annotation { "Feature Type Name" : "Feature", "Feature Type Description" : "" }
export const myFeature = defineFeature(function(context is Context, id is Id, definition is map)
    precondition{}
    {
        {
            var Q0;
            Q0=qCreatedBy(makeId("Top.planeOp"),FACE);
            var sketch = newSketch(context, id + "F0", { "sketchPlane" : qUnion([Q0])});
            skLineSegment(sketch, "E0.bottom", {"start": v(15000, -25000) * mm, "end": v(-15000, -25000) * mm});
            skLineSegment(sketch, "E0.top", {"start": v(15000, 25000) * mm, "end": v(-15000, 25000) * mm});
            skLineSegment(sketch, "E0.left", {"start": v(15000, -25000) * mm, "end": v(15000, 25000) * mm});
            skLineSegment(sketch, "E0.right", {"start": v(-15000, -25000) * mm, "end": v(-15000, 25000) * mm});
            skPoint(sketch, "E0.middle", {"position": v(0, 0) * mm});
            skSolve(sketch);
        }
        {
            var Q0;
            Q0=makeQuery(id+"F0.imprint","IMPRINT",FACE,{"disambiguationData":[TD([[makeQuery(id+"F0.imprint","IMPRINT",EDGE,{"derivedFrom":sQuery(id+"F0.wireOp",EDGE,"E0.bottom")}),-1.0]])]});
            var Q1;
            Q1=makeQuery(id+"F0.imprint","IMPRINT",FACE,{"disambiguationData":[TD([[makeQuery(id+"F0.imprint","IMPRINT",EDGE,{"derivedFrom":makeQuery(id+"F2.imprint","IMPRINT",EDGE,{"derivedFrom":sQuery(id+"F2.wireOp",EDGE,"E106.sketch_text.stroke-0")})}),-1.0]])]});
            var Q2;
            Q2=makeQuery(id+"F0.imprint","IMPRINT",FACE,{"disambiguationData":[TD([[makeQuery(id+"F0.imprint","IMPRINT",EDGE,{"derivedFrom":makeQuery(id+"F2.imprint","IMPRINT",EDGE,{"derivedFrom":sQuery(id+"F2.wireOp",EDGE,"E106.sketch_text.stroke-63")})}),-1.0]])]});
            var Q3;
            {var subQ5=sQuery(id+"F2.wireOp",EDGE,"E23");Q3=makeQuery(id+"F0.imprint","IMPRINT",FACE,{"disambiguationData":[TD([[makeQuery(id+"F0.imprint","IMPRINT",EDGE,{"derivedFrom":makeQuery(id+"F2.imprint","IMPRINT",EDGE,{"derivedFrom":subQ5})}),-1.0]])]});}
            var Q4;
            Q4=makeQuery(id+"F0.imprint","IMPRINT",FACE,{"disambiguationData":[TD([[makeQuery(id+"F0.imprint","IMPRINT",EDGE,{"derivedFrom":makeQuery(id+"F2.imprint","IMPRINT",EDGE,{"derivedFrom":sQuery(id+"F2.wireOp",EDGE,"E106.sketch_text.stroke-110")})}),-1.0]])]});
            var Q5;
            Q5=makeQuery(id+"F0.imprint","IMPRINT",FACE,{"disambiguationData":[TD([[makeQuery(id+"F0.imprint","IMPRINT",EDGE,{"derivedFrom":makeQuery(id+"F2.imprint","IMPRINT",EDGE,{"derivedFrom":sQuery(id+"F2.wireOp",EDGE,"E106.sketch_text.stroke-133")})}),-1.0]])]});
            var Q6;
            Q6=makeQuery(id+"F0.imprint","IMPRINT",FACE,{"disambiguationData":[TD([[makeQuery(id+"F0.imprint","IMPRINT",EDGE,{"derivedFrom":makeQuery(id+"F2.imprint","IMPRINT",EDGE,{"derivedFrom":sQuery(id+"F2.wireOp",EDGE,"E106.sketch_text.stroke-137")})}),-1.0]])]});
            var Q7;
            Q7=makeQuery(id+"F0.imprint","IMPRINT",FACE,{"disambiguationData":[TD([[makeQuery(id+"F0.imprint","IMPRINT",EDGE,{"derivedFrom":makeQuery(id+"F2.imprint","IMPRINT",EDGE,{"derivedFrom":sQuery(id+"F2.wireOp",EDGE,"E106.sketch_text.stroke-82")})}),-1.0]])]});
            var Q8;
            Q8=makeQuery(id+"F0.imprint","IMPRINT",FACE,{"disambiguationData":[TD([[makeQuery(id+"F0.imprint","IMPRINT",EDGE,{"derivedFrom":makeQuery(id+"F2.imprint","IMPRINT",EDGE,{"derivedFrom":sQuery(id+"F2.wireOp",EDGE,"E106.sketch_text.stroke-38")})}),-1.0]])]});
            var Q9;
            Q9=makeQuery(id+"F0.imprint","IMPRINT",FACE,{"disambiguationData":[TD([[makeQuery(id+"F0.imprint","IMPRINT",EDGE,{"derivedFrom":makeQuery(id+"F2.imprint","IMPRINT",EDGE,{"derivedFrom":sQuery(id+"F2.wireOp",EDGE,"E106.sketch_text.stroke-13")})}),-1.0]])]});
            extrude(context, id + "F1", {"entities" : qUnion([Q0, Q1, Q2, Q3, Q4, Q5, Q6, Q7, Q8, Q9]), "oppositeDirection" : true, "depth" : 25 * mm, "offsetDistance" : 25 * mm});
        }
        {
            var Q0;
            Q0=qCreatedBy(makeId("Top.planeOp"),FACE);
            var sketch = newSketch(context, id + "F2", { "sketchPlane" : qUnion([Q0])});
            skLineSegment(sketch, "E1.bottom", {"start": v(15000, -25000) * mm, "end": v(-15000, -25000) * mm});
            skLineSegment(sketch, "E1.top", {"start": v(15000, 25000) * mm, "end": v(-15000, 25000) * mm});
            skLineSegment(sketch, "E1.left", {"start": v(15000, -25000) * mm, "end": v(15000, 25000) * mm});
            skLineSegment(sketch, "E1.right", {"start": v(-15000, -25000) * mm, "end": v(-15000, -18414.08) * mm});
            skPoint(sketch, "E1.middle", {"position": v(0, 0) * mm});
            skLineSegment(sketch, "E2", {"start": v(15000, 1000) * mm, "end": v(9000, 1000) * mm});
            skLineSegment(sketch, "E3", {"start": v(12185.8, -25000) * mm, "end": v(12185.8, 25000) * mm});
            skLineSegment(sketch, "E4.0", {"start": v(11500, -25000) * mm, "end": v(11500, 25000) * mm});
            skLineSegment(sketch, "E5", {"start": v(9000, -11000) * mm, "end": v(9000, 1000) * mm});
            skLineSegment(sketch, "E6", {"start": v(9000, 1000) * mm, "end": v(9000, 25000) * mm});
            skText(sketch, "E7", { "text": "Weld", "fontName": "OpenSans-Regular.ttf"});
            skText(sketch, "E8", { "text": "Blast", "fontName": "OpenSans-Regular.ttf"});
            skText(sketch, "E9", { "text": "Paint", "fontName": "OpenSans-Regular.ttf"});
            skLineSegment(sketch, "E10", {"start": v(7800, 25000) * mm, "end": v(7800, -25000) * mm});
            skPoint(sketch, "E11.orphan", {"position": v(7800, 25000) * mm});
            skText(sketch, "E12", { "text": "Dock", "fontName": "OpenSans-Regular.ttf"});
            skLineSegment(sketch, "E13", {"start": v(9000, 13000) * mm, "end": v(15000, 13000) * mm});
            skLineSegment(sketch, "E14", {"start": v(3200, 25000) * mm, "end": v(3200, 9000) * mm});
            skPoint(sketch, "E15", {"position": v(800, -25000) * mm});
            skPoint(sketch, "E16", {"position": v(5500, -25000) * mm});
            skLineSegment(sketch, "E17", {"start": v(5157.1, -25000) * mm, "end": v(5157.1, 9000) * mm});
            skLineSegment(sketch, "E18.0", {"start": v(5842.9, -25000) * mm, "end": v(5842.9, 9000) * mm});
            skLineSegment(sketch, "E19.0", {"start": v(-400, 7800) * mm, "end": v(7800, 7800) * mm});
            skPoint(sketch, "E20", {"position": v(-1414.44, -25000) * mm});
            skLineSegment(sketch, "E21", {"start": v(9000, -11000) * mm, "end": v(15000, -11000) * mm});
            skLineSegment(sketch, "E22", {"start": v(-1414.44, -25000) * mm, "end": v(-1414.44, 7800) * mm});
            skLineSegment(sketch, "E23", {"start": v(-1414.44, 7800) * mm, "end": v(-400, 7800) * mm});
            skLineSegment(sketch, "E24.0", {"start": v(-2614.44, -25000) * mm, "end": v(-2614.44, -10700) * mm});
            skLineSegment(sketch, "E25.trimOffspring", {"start": v(3200, 9000) * mm, "end": v(7800, 9000) * mm});
            skPoint(sketch, "E26", {"position": v(-1414.44, -8600) * mm});
            skPoint(sketch, "E27", {"position": v(-1414.44, -8000) * mm});
            skLineSegment(sketch, "E28", {"start": v(-1414.44, -8000) * mm, "end": v(7800, -8000) * mm});
            skLineSegment(sketch, "E29.0", {"start": v(-1414.44, -9200) * mm, "end": v(7800, -9200) * mm});
            skPoint(sketch, "E30", {"position": v(5500, -23850) * mm});
            skLineSegment(sketch, "E31", {"start": v(5500, -23850) * mm, "end": v(4500, -23850) * mm});
            skLineSegment(sketch, "E32", {"start": v(5500, -23850) * mm, "end": v(7500, -23850) * mm});
            skLineSegment(sketch, "E33", {"start": v(4500, -23850) * mm, "end": v(4500, -10350) * mm});
            skLineSegment(sketch, "E34", {"start": v(7500, -23850) * mm, "end": v(7500, -10350) * mm});
            skLineSegment(sketch, "E35", {"start": v(7500, -10350) * mm, "end": v(4500, -10350) * mm});
            skLineSegment(sketch, "E36", {"start": v(-10000, 25000) * mm, "end": v(-10000, 20000) * mm});
            skLineSegment(sketch, "E37", {"start": v(-10000, 20000) * mm, "end": v(-15000, 20000) * mm});
            skText(sketch, "E38", { "text": "Plas", "fontName": "OpenSans-Regular.ttf"});
            skLineSegment(sketch, "E39", {"start": v(-7000, 25000) * mm, "end": v(-7000, 22000) * mm});
            skLineSegment(sketch, "E40", {"start": v(-7000, 22000) * mm, "end": v(-10000, 22000) * mm});
            skText(sketch, "E41", { "text": "Sht.", "fontName": "OpenSans-Regular.ttf"});
            skLineSegment(sketch, "E42", {"start": v(-7000, 22000) * mm, "end": v(-7000, 20000) * mm});
            skLineSegment(sketch, "E43", {"start": v(-15000, 17800) * mm, "end": v(-2452.25, 17800) * mm});
            skLineSegment(sketch, "E44", {"start": v(-10000, 20000) * mm, "end": v(-7000, 20000) * mm});
            skText(sketch, "E45", { "text": "Scp", "fontName": "OpenSans-Regular.ttf"});
            skPoint(sketch, "E46", {"position": v(-15000, 19325) * mm});
            skPoint(sketch, "E47", {"position": v(-15000, 18475) * mm});
            skLineSegment(sketch, "E48", {"start": v(-15000, 18475) * mm, "end": v(-15850, 18475) * mm, "construction": true});
            skArc(sketch, "E49", {"start": v(-15850, 18475) * mm, "mid": v(-15601.04, 19076.04) * mm, "end": v(-15000, 19325) * mm, "construction": true});
            skPoint(sketch, "E50", {"position": v(7975, 25000) * mm});
            skPoint(sketch, "E51", {"position": v(8825, 25000) * mm});
            skLineSegment(sketch, "E52", {"start": v(7975, 25000) * mm, "end": v(7975, 25850) * mm, "construction": true});
            skArc(sketch, "E53", {"start": v(7975, 25850) * mm, "mid": v(8576.04, 25601.04) * mm, "end": v(8825, 25000) * mm, "construction": true});
            skPoint(sketch, "E54", {"position": v(9500, 13000) * mm});
            skPoint(sketch, "E55", {"position": v(14500, 13000) * mm});
            skLineSegment(sketch, "E56", {"start": v(14500, 12500) * mm, "end": v(14500, 13500) * mm, "construction": true});
            skLineSegment(sketch, "E57", {"start": v(9500, 12500) * mm, "end": v(9500, 13500) * mm, "construction": true});
            skLineSegment(sketch, "E58", {"start": v(14500, 24500) * mm, "end": v(14500, 25500) * mm, "construction": true});
            skPoint(sketch, "E59", {"position": v(14500, 25000) * mm});
            skPoint(sketch, "E60", {"position": v(9500, 25000) * mm});
            skLineSegment(sketch, "E61", {"start": v(9500, 24500) * mm, "end": v(9500, 25500) * mm, "construction": true});
            skPoint(sketch, "E62", {"position": v(4200, 25000) * mm});
            skPoint(sketch, "E63", {"position": v(6800, 25000) * mm});
            skLineSegment(sketch, "E64", {"start": v(4200, 24500) * mm, "end": v(4200, 25500) * mm, "construction": true});
            skLineSegment(sketch, "E65", {"start": v(6800, 25000) * mm, "end": v(6800, 24500) * mm, "construction": true});
            skLineSegment(sketch, "E66", {"start": v(6800, 24500) * mm, "end": v(6800, 25500) * mm, "construction": true});
            skLineSegment(sketch, "E67.0", {"start": v(12260.8, -25000) * mm, "end": v(12260.8, 25000) * mm});
            skLineSegment(sketch, "E68.0", {"start": v(11425, -25000) * mm, "end": v(11425, 25000) * mm});
            skLineSegment(sketch, "E69.0", {"start": v(5917.9, -25000) * mm, "end": v(5917.9, 9000) * mm});
            skLineSegment(sketch, "E70.0", {"start": v(5082.1, -25000) * mm, "end": v(5082.1, 9000) * mm});
            skLineSegment(sketch, "E71", {"start": v(-4100.12, 13300) * mm, "end": v(-6825.09, 13300) * mm});
            skPoint(sketch, "E72", {"position": v(-6200, 15550) * mm});
            skLineSegment(sketch, "E73", {"start": v(-6200, 14010) * mm, "end": v(-6200, 17090) * mm});
            skLineSegment(sketch, "E74", {"start": v(-6200, 17090) * mm, "end": v(-8500, 17090) * mm});
            skLineSegment(sketch, "E75", {"start": v(-8500, 17090) * mm, "end": v(-8500, 14010) * mm});
            skLineSegment(sketch, "E76", {"start": v(-8500, 14010) * mm, "end": v(-6200, 14010) * mm});
            skPoint(sketch, "E77", {"position": v(-8500, 15550) * mm});
            skText(sketch, "E78", { "text": "B.Saw", "fontName": "OpenSans-Regular.ttf"});
            skLineSegment(sketch, "E79", {"start": v(-8500, 16050) * mm, "end": v(-14500, 16050) * mm});
            skLineSegment(sketch, "E80", {"start": v(-14500, 16050) * mm, "end": v(-14500, 15550) * mm});
            skLineSegment(sketch, "E81", {"start": v(-14500, 15550) * mm, "end": v(-14500, 15050) * mm});
            skLineSegment(sketch, "E82", {"start": v(-14500, 15050) * mm, "end": v(-8500, 15050) * mm});
            skLineSegment(sketch, "E83", {"start": v(-6200, 16050) * mm, "end": v(-3000, 16050) * mm});
            skLineSegment(sketch, "E84", {"start": v(-6200, 15050) * mm, "end": v(-3000, 15050) * mm});
            skLineSegment(sketch, "E85", {"start": v(-3000, 15050) * mm, "end": v(-3000, 16050) * mm});
            skLineSegment(sketch, "E86", {"start": v(-15000, 9900) * mm, "end": v(-4100.12, 9900) * mm});
            skLineSegment(sketch, "E87", {"start": v(-4100.12, 9900) * mm, "end": v(-4100.12, 13300) * mm});
            skLineSegment(sketch, "E88", {"start": v(-9550.06, 13300) * mm, "end": v(-9550.06, 9900) * mm});
            skLineSegment(sketch, "E89", {"start": v(-9550.06, 13300) * mm, "end": v(-15000, 13300) * mm});
            skLineSegment(sketch, "E90", {"start": v(-6825.09, 13300) * mm, "end": v(-6825.09, 9900) * mm});
            skLineSegment(sketch, "E91", {"start": v(-6825.09, 13300) * mm, "end": v(-9550.06, 13300) * mm});
            skText(sketch, "E92", { "text": "Mess", "fontName": "OpenSans-Regular.ttf"});
            skText(sketch, "E93", { "text": "Office", "fontName": "OpenSans-Regular.ttf"});
            skText(sketch, "E94", { "text": "Office", "fontName": "OpenSans-Regular.ttf"});
            skLineSegment(sketch, "E95", {"start": v(-15000, 5100) * mm, "end": v(-10300, 5100) * mm});
            skLineSegment(sketch, "E96", {"start": v(-15000, 1300) * mm, "end": v(-2614.44, 1300) * mm});
            skLineSegment(sketch, "E97", {"start": v(-10300, 5100) * mm, "end": v(-10300, 1300) * mm});
            skText(sketch, "E98", { "text": "Abolutions", "fontName": "OpenSans-Regular.ttf"});
            skLineSegment(sketch, "E99", {"start": v(-5176.3, 5100) * mm, "end": v(-5176.3, 1300) * mm});
            skLineSegment(sketch, "E100", {"start": v(-7738.15, 5100) * mm, "end": v(-5176.3, 5100) * mm});
            skLineSegment(sketch, "E101", {"start": v(-10300, 5100) * mm, "end": v(-7738.15, 5100) * mm});
            skLineSegment(sketch, "E102", {"start": v(-5176.3, 5100) * mm, "end": v(-2614.44, 5100) * mm});
            skText(sketch, "E103", { "text": "Nut & Bolt", "fontName": "OpenSans-Regular.ttf"});
            skText(sketch, "E104", { "text": "Tools", "fontName": "OpenSans-Regular.ttf"});
            skPoint(sketch, "E105.end.orphan", {"position": v(9000, -25000) * mm});
            skText(sketch, "E106", { "text": "Assembly", "fontName": "OpenSans-Regular.ttf"});
            skText(sketch, "E107", { "text": "Maint. Pit", "fontName": "OpenSans-Regular.ttf"});
            skLineSegment(sketch, "E108", {"start": v(9000, -11000) * mm, "end": v(9000, -25000) * mm});
            skLineSegment(sketch, "E109", {"start": v(-15000, 8700) * mm, "end": v(-2614.44, 8700) * mm});
            skLineSegment(sketch, "E110", {"start": v(-2614.44, 8700) * mm, "end": v(-2614.44, 1300) * mm});
            skLineSegment(sketch, "E111", {"start": v(-15000, 6300) * mm, "end": v(-2614.44, 6300) * mm});
            skPoint(sketch, "E112.orphan", {"position": v(-4100.12, 5100) * mm});
            skPoint(sketch, "E113.secondSnap0", {"position": v(-7000, 23500) * mm});
            skLineSegment(sketch, "E114.bottom", {"start": v(-15000, 1300) * mm, "end": v(-14380, 1300) * mm});
            skLineSegment(sketch, "E115.bottom", {"start": v(-13364.3, 1300) * mm, "end": v(-11864.3, 1300) * mm});
            skLineSegment(sketch, "E116", {"start": v(-15000, 100) * mm, "end": v(-8650.54, 100) * mm});
            skLineSegment(sketch, "E117", {"start": v(-8650.54, 100) * mm, "end": v(-2614.44, 100) * mm});
            skLineSegment(sketch, "E118.bottom", {"start": v(-12122.81, -190.8) * mm, "end": v(-9622.81, -190.8) * mm});
            skLineSegment(sketch, "E118.top", {"start": v(-12122.81, -5370.8) * mm, "end": v(-9622.81, -5370.8) * mm});
            skLineSegment(sketch, "E118.left", {"start": v(-12122.81, -190.8) * mm, "end": v(-12122.81, -5370.8) * mm});
            skLineSegment(sketch, "E118.right", {"start": v(-9622.81, -190.8) * mm, "end": v(-9622.81, -5370.8) * mm});
            skText(sketch, "E119", { "text": "W/Turn NC", "fontName": "OpenSans-Regular.ttf"});
            skLineSegment(sketch, "E120", {"start": v(-9194.98, 100) * mm, "end": v(-9194.98, -5370.8) * mm, "construction": true});
            skLineSegment(sketch, "E121.bottom", {"start": v(-7683.51, -883.35) * mm, "end": v(-6183.51, -883.35) * mm});
            skLineSegment(sketch, "E121.top", {"start": v(-7683.51, -4333.35) * mm, "end": v(-6183.51, -4333.35) * mm});
            skLineSegment(sketch, "E121.left", {"start": v(-7683.51, -883.35) * mm, "end": v(-7683.51, -4333.35) * mm});
            skLineSegment(sketch, "E121.right", {"start": v(-6183.51, -883.35) * mm, "end": v(-6183.51, -4333.35) * mm});
            skLineSegment(sketch, "E122", {"start": v(-5874.17, 100) * mm, "end": v(-5874.17, -5370.8) * mm, "construction": true});
            skText(sketch, "E123", { "text": "6ft N/C", "fontName": "OpenSans-Regular.ttf"});
            skLineSegment(sketch, "E124.bottom", {"start": v(-4825.61, -1295.66) * mm, "end": v(-3335.61, -1295.66) * mm});
            skLineSegment(sketch, "E124.top", {"start": v(-4825.61, -3265.66) * mm, "end": v(-3335.61, -3265.66) * mm});
            skLineSegment(sketch, "E124.left", {"start": v(-4825.61, -1295.66) * mm, "end": v(-4825.61, -3265.66) * mm});
            skLineSegment(sketch, "E124.right", {"start": v(-3335.61, -1295.66) * mm, "end": v(-3335.61, -3265.66) * mm});
            skLineSegment(sketch, "E125", {"start": v(-15000, -5900) * mm, "end": v(-2614.44, -5900) * mm});
            skLineSegment(sketch, "E126", {"start": v(-15000, -7100) * mm, "end": v(-10032.4, -7100) * mm});
            skLineSegment(sketch, "E127.bottom", {"start": v(-3107.2, -7667.25) * mm, "end": v(-4207.2, -7667.25) * mm});
            skLineSegment(sketch, "E127.top", {"start": v(-3107.2, -9167.25) * mm, "end": v(-4207.2, -9167.25) * mm});
            skLineSegment(sketch, "E127.left", {"start": v(-3107.2, -7667.25) * mm, "end": v(-3107.2, -9167.25) * mm});
            skLineSegment(sketch, "E127.right", {"start": v(-4207.2, -7667.25) * mm, "end": v(-4207.2, -9167.25) * mm});
            skText(sketch, "E128", { "text": "4 Ft", "fontName": "OpenSans-Regular.ttf"});
            skLineSegment(sketch, "E129.bottom", {"start": v(-5041.59, -7682.06) * mm, "end": v(-6241.59, -7682.06) * mm});
            skLineSegment(sketch, "E129.top", {"start": v(-5041.59, -9182.06) * mm, "end": v(-6241.59, -9182.06) * mm});
            skLineSegment(sketch, "E129.left", {"start": v(-5041.59, -7682.06) * mm, "end": v(-5041.59, -9182.06) * mm});
            skLineSegment(sketch, "E129.right", {"start": v(-6241.59, -7682.06) * mm, "end": v(-6241.59, -9182.06) * mm});
            skText(sketch, "E130", { "text": "B", "fontName": "OpenSans-Regular.ttf"});
            skLineSegment(sketch, "E131.bottom", {"start": v(-6955.24, -7425.03) * mm, "end": v(-8479.24, -7425.03) * mm});
            skLineSegment(sketch, "E131.top", {"start": v(-6955.24, -9203.03) * mm, "end": v(-8479.24, -9203.03) * mm});
            skLineSegment(sketch, "E131.left", {"start": v(-6955.24, -7425.03) * mm, "end": v(-6955.24, -9203.03) * mm});
            skLineSegment(sketch, "E131.right", {"start": v(-8479.24, -7425.03) * mm, "end": v(-8479.24, -9203.03) * mm});
            skText(sketch, "E132", { "text": "BP", "fontName": "OpenSans-Regular.ttf"});
            skLineSegment(sketch, "E133", {"start": v(-8832.4, -7100) * mm, "end": v(-8832.4, -9500) * mm});
            skLineSegment(sketch, "E134", {"start": v(-8832.4, -9500) * mm, "end": v(-2614.44, -9500) * mm});
            skLineSegment(sketch, "E135", {"start": v(-10032.4, -7100) * mm, "end": v(-10032.4, -10700) * mm});
            skLineSegment(sketch, "E136", {"start": v(-8832.4, -10700) * mm, "end": v(-2614.44, -10700) * mm});
            skLineSegment(sketch, "E137.bottom", {"start": v(-14293.59, -7777.48) * mm, "end": v(-10693.59, -7777.48) * mm});
            skLineSegment(sketch, "E137.top", {"start": v(-14293.59, -11377.48) * mm, "end": v(-10693.59, -11377.48) * mm});
            skLineSegment(sketch, "E137.left", {"start": v(-14293.59, -7777.48) * mm, "end": v(-14293.59, -11377.48) * mm});
            skLineSegment(sketch, "E137.right", {"start": v(-10693.59, -7777.48) * mm, "end": v(-10693.59, -11377.48) * mm});
            skLineSegment(sketch, "E138.trimOffspring", {"start": v(-8832.4, -7100) * mm, "end": v(-2614.44, -7100) * mm});
            skLineSegment(sketch, "E139.trimOffspring", {"start": v(-2614.44, -5900) * mm, "end": v(-2614.44, 1300) * mm});
            skLineSegment(sketch, "E140.trimOffspring", {"start": v(-2614.44, -9500) * mm, "end": v(-2614.44, -7100) * mm});
            skText(sketch, "E141", { "text": "VMC", "fontName": "OpenSans-Regular.ttf"});
            skLineSegment(sketch, "E142.bottom", {"start": v(-15000, -11815.23) * mm, "end": v(-14000, -11815.23) * mm});
            skLineSegment(sketch, "E142.top", {"start": v(-15000, -13815.23) * mm, "end": v(-14000, -13815.23) * mm});
            skLineSegment(sketch, "E142.left", {"start": v(-15000, -11815.23) * mm, "end": v(-15000, -13815.23) * mm});
            skLineSegment(sketch, "E142.right", {"start": v(-14000, -11815.23) * mm, "end": v(-14000, -13815.23) * mm});
            skText(sketch, "E143", { "text": "B", "fontName": "OpenSans-Regular.ttf"});
            skLineSegment(sketch, "E144", {"start": v(-8832.4, -10700) * mm, "end": v(-8832.4, -14114.08) * mm});
            skLineSegment(sketch, "E145", {"start": v(-10032.4, -10700) * mm, "end": v(-10032.4, -12914.08) * mm});
            skLineSegment(sketch, "E146", {"start": v(-10032.4, -12914.08) * mm, "end": v(-13218.84, -12914.08) * mm});
            skLineSegment(sketch, "E147", {"start": v(-13218.84, -12914.08) * mm, "end": v(-13218.84, -14114.08) * mm});
            skLineSegment(sketch, "E148", {"start": v(-13218.84, -14114.08) * mm, "end": v(-8832.4, -14114.08) * mm});
            skLineSegment(sketch, "E149.bottom", {"start": v(-8412.36, -11710.95) * mm, "end": v(-7392.36, -11710.95) * mm});
            skLineSegment(sketch, "E149.top", {"start": v(-8412.36, -13410.95) * mm, "end": v(-7392.36, -13410.95) * mm});
            skLineSegment(sketch, "E149.left", {"start": v(-8412.36, -11710.95) * mm, "end": v(-8412.36, -13410.95) * mm});
            skLineSegment(sketch, "E149.right", {"start": v(-7392.36, -11710.95) * mm, "end": v(-7392.36, -13410.95) * mm});
            skText(sketch, "E150", { "text": "R", "fontName": "OpenSans-Regular.ttf"});
            skLineSegment(sketch, "E151.bottom", {"start": v(-6482.85, -11468.66) * mm, "end": v(-5482.85, -11468.66) * mm});
            skLineSegment(sketch, "E151.top", {"start": v(-6482.85, -13468.66) * mm, "end": v(-5482.85, -13468.66) * mm});
            skLineSegment(sketch, "E151.left", {"start": v(-6482.85, -11468.66) * mm, "end": v(-6482.85, -13468.66) * mm});
            skLineSegment(sketch, "E151.right", {"start": v(-5482.85, -11468.66) * mm, "end": v(-5482.85, -13468.66) * mm});
            skText(sketch, "E152", { "text": "B", "fontName": "OpenSans-Regular.ttf"});
            skLineSegment(sketch, "E153.bottom", {"start": v(-4462.03, -11541.38) * mm, "end": v(-2938.03, -11541.38) * mm});
            skLineSegment(sketch, "E153.top", {"start": v(-4462.03, -13319.38) * mm, "end": v(-2938.03, -13319.38) * mm});
            skLineSegment(sketch, "E153.left", {"start": v(-4462.03, -11541.38) * mm, "end": v(-4462.03, -13319.38) * mm});
            skLineSegment(sketch, "E153.right", {"start": v(-2938.03, -11541.38) * mm, "end": v(-2938.03, -13319.38) * mm});
            skText(sketch, "E154", { "text": "N/C\nB/P", "fontName": "OpenSans-Regular.ttf"});
            skLineSegment(sketch, "E155.bottom", {"start": v(3200, 25000) * mm, "end": v(700, 25000) * mm});
            skLineSegment(sketch, "E155.top", {"start": v(3200, 19000) * mm, "end": v(700, 19000) * mm});
            skLineSegment(sketch, "E155.left", {"start": v(3200, 25000) * mm, "end": v(3200, 19000) * mm});
            skLineSegment(sketch, "E155.right", {"start": v(700, 25000) * mm, "end": v(700, 19000) * mm});
            skLineSegment(sketch, "E156.bottom", {"start": v(-500, 25000) * mm, "end": v(-3000, 25000) * mm});
            skLineSegment(sketch, "E156.top", {"start": v(-500, 19000) * mm, "end": v(-3000, 19000) * mm});
            skLineSegment(sketch, "E156.left", {"start": v(-500, 25000) * mm, "end": v(-500, 19000) * mm});
            skLineSegment(sketch, "E156.right", {"start": v(-3000, 25000) * mm, "end": v(-3000, 19000) * mm});
            skLineSegment(sketch, "E157.bottom", {"start": v(-7000, 25000) * mm, "end": v(-4500, 25000) * mm});
            skLineSegment(sketch, "E157.top", {"start": v(-7000, 19000) * mm, "end": v(-4500, 19000) * mm});
            skLineSegment(sketch, "E157.left", {"start": v(-7000, 25000) * mm, "end": v(-7000, 19000) * mm});
            skLineSegment(sketch, "E157.right", {"start": v(-4500, 25000) * mm, "end": v(-4500, 19000) * mm});
            skLineSegment(sketch, "E158", {"start": v(-2452.25, 17800) * mm, "end": v(-2452.25, 13300) * mm});
            skLineSegment(sketch, "E159", {"start": v(-2452.25, 13300) * mm, "end": v(-4100.12, 13300) * mm});
            skPoint(sketch, "E160.orphan", {"position": v(-4100, 17800) * mm});
            skLineSegment(sketch, "E161.bottom", {"start": v(3200, 17800) * mm, "end": v(700, 17800) * mm});
            skLineSegment(sketch, "E161.top", {"start": v(3200, 11800) * mm, "end": v(700, 11800) * mm});
            skLineSegment(sketch, "E161.left", {"start": v(3200, 17800) * mm, "end": v(3200, 11800) * mm});
            skLineSegment(sketch, "E161.right", {"start": v(700, 17800) * mm, "end": v(700, 11800) * mm});
            skText(sketch, "E162", { "text": "Dbl. Steel", "fontName": "OpenSans-Regular.ttf"});
            skText(sketch, "E163", { "text": "Dbl. Steel", "fontName": "OpenSans-Regular.ttf"});
            skText(sketch, "E164", { "text": "Dbl. Steel", "fontName": "OpenSans-Regular.ttf"});
            skText(sketch, "E165", { "text": "Dbl. Steel", "fontName": "OpenSans-Regular.ttf"});
            skLineSegment(sketch, "E166", {"start": v(-4100.12, 9900) * mm, "end": v(-1414.44, 9900) * mm});
            skLineSegment(sketch, "E167", {"start": v(-1414.44, 9900) * mm, "end": v(-1414.44, 9000) * mm});
            skLineSegment(sketch, "E168", {"start": v(-1414.44, 9000) * mm, "end": v(3200, 9000) * mm});
            skText(sketch, "E169", { "text": "M/C", "fontName": "OpenSans-Regular.ttf"});
            skLineSegment(sketch, "E170", {"start": v(-7128.66, 1300) * mm, "end": v(-7128.66, 100) * mm});
            skText(sketch, "E171", { "text": "Stairs", "fontName": "OpenSans-Regular.ttf"});
            skLineSegment(sketch, "E172", {"start": v(-13218.84, -14114.08) * mm, "end": v(-15000, -14114.08) * mm});
            skLineSegment(sketch, "E173", {"start": v(-8832.4, -14114.08) * mm, "end": v(-2614.44, -14114.08) * mm});
            skLineSegment(sketch, "E174", {"start": v(-15000, -18414.08) * mm, "end": v(-2614.44, -18414.08) * mm});
            skLineSegment(sketch, "E175.bottom", {"start": v(-14600, -14564.08) * mm, "end": v(-11820, -14564.08) * mm});
            skLineSegment(sketch, "E175.top", {"start": v(-14600, -17964.08) * mm, "end": v(-11820, -17964.08) * mm});
            skLineSegment(sketch, "E175.left", {"start": v(-14600, -14564.08) * mm, "end": v(-14600, -17964.08) * mm});
            skLineSegment(sketch, "E175.right", {"start": v(-11820, -14564.08) * mm, "end": v(-11820, -17964.08) * mm});
            skLineSegment(sketch, "E176", {"start": v(-15000, -14114.08) * mm, "end": v(-15000, 25000) * mm});
            skLineSegment(sketch, "E177", {"start": v(-15000, -18414.08) * mm, "end": v(-15000, -14114.08) * mm});
            skLineSegment(sketch, "E178", {"start": v(-14600, -16264.08) * mm, "end": v(-15000, -16264.08) * mm, "construction": true});
            skText(sketch, "E179", { "text": "S/G", "fontName": "OpenSans-Regular.ttf"});
            skLineSegment(sketch, "E180.bottom", {"start": v(-9854, -17356.39) * mm, "end": v(-8204, -17356.39) * mm});
            skLineSegment(sketch, "E180.top", {"start": v(-9854, -18206.39) * mm, "end": v(-8204, -18206.39) * mm});
            skLineSegment(sketch, "E180.left", {"start": v(-9854, -17356.39) * mm, "end": v(-9854, -18206.39) * mm});
            skLineSegment(sketch, "E180.right", {"start": v(-8204, -17356.39) * mm, "end": v(-8204, -18206.39) * mm});
            skText(sketch, "E181", { "text": "S/G", "fontName": "OpenSans-Regular.ttf"});
            skLineSegment(sketch, "E182.bottom", {"start": v(-9259.14, -14424.68) * mm, "end": v(-6459.14, -14424.68) * mm});
            skLineSegment(sketch, "E182.top", {"start": v(-9259.14, -15624.68) * mm, "end": v(-6459.14, -15624.68) * mm});
            skLineSegment(sketch, "E182.left", {"start": v(-9259.14, -14424.68) * mm, "end": v(-9259.14, -15624.68) * mm});
            skLineSegment(sketch, "E182.right", {"start": v(-6459.14, -14424.68) * mm, "end": v(-6459.14, -15624.68) * mm});
            skText(sketch, "E183", { "text": "Cyl.", "fontName": "OpenSans-Regular.ttf"});
            skLineSegment(sketch, "E184.bottom", {"start": v(-3124.14, -15799.31) * mm, "end": v(-5124.14, -15799.31) * mm});
            skLineSegment(sketch, "E184.top", {"start": v(-3124.14, -17799.31) * mm, "end": v(-5124.14, -17799.31) * mm});
            skLineSegment(sketch, "E184.left", {"start": v(-3124.14, -15799.31) * mm, "end": v(-3124.14, -17799.31) * mm});
            skLineSegment(sketch, "E184.right", {"start": v(-5124.14, -15799.31) * mm, "end": v(-5124.14, -17799.31) * mm});
            skText(sketch, "E185", { "text": "T&C", "fontName": "OpenSans-Regular.ttf"});
            skText(sketch, "E186", { "text": "Grinding Cell", "fontName": "OpenSans-Italic.ttf"});
            skText(sketch, "E187", { "text": "Machine Shop", "fontName": "OpenSans-Italic.ttf"});
            skLineSegment(sketch, "E188.bottom", {"start": v(-10615.85, -18819.14) * mm, "end": v(-3315.85, -18819.14) * mm});
            skLineSegment(sketch, "E188.top", {"start": v(-10615.85, -20819.14) * mm, "end": v(-3315.85, -20819.14) * mm});
            skLineSegment(sketch, "E188.left", {"start": v(-10615.85, -18819.14) * mm, "end": v(-10615.85, -20819.14) * mm});
            skLineSegment(sketch, "E188.right", {"start": v(-3315.85, -18819.14) * mm, "end": v(-3315.85, -20819.14) * mm});
            skText(sketch, "E189", { "text": "Wheel Press", "fontName": "OpenSans-Regular.ttf"});
            skLineSegment(sketch, "E190.bottom", {"start": v(-14211.47, -22836.57) * mm, "end": v(-9211.47, -22836.57) * mm});
            skLineSegment(sketch, "E190.top", {"start": v(-14211.47, -24836.57) * mm, "end": v(-9211.47, -24836.57) * mm});
            skLineSegment(sketch, "E190.left", {"start": v(-14211.47, -22836.57) * mm, "end": v(-14211.47, -24836.57) * mm});
            skLineSegment(sketch, "E190.right", {"start": v(-9211.47, -22836.57) * mm, "end": v(-9211.47, -24836.57) * mm});
            skText(sketch, "E191", { "text": "Furnace", "fontName": "OpenSans-Regular.ttf"});
            skLineSegment(sketch, "E192.bottom", {"start": v(-7920.13, -23823) * mm, "end": v(-3920.13, -23823) * mm});
            skLineSegment(sketch, "E192.top", {"start": v(-7920.13, -24823) * mm, "end": v(-3920.13, -24823) * mm});
            skLineSegment(sketch, "E192.left", {"start": v(-7920.13, -23823) * mm, "end": v(-7920.13, -24823) * mm});
            skLineSegment(sketch, "E192.right", {"start": v(-3920.13, -23823) * mm, "end": v(-3920.13, -24823) * mm});
            skText(sketch, "E193", { "text": "Quench", "fontName": "OpenSans-Regular.ttf"});
            skLineSegment(sketch, "E194.bottom", {"start": v(-14518.37, -18889.75) * mm, "end": v(-11518.37, -18889.75) * mm});
            skLineSegment(sketch, "E194.top", {"start": v(-14518.37, -20889.75) * mm, "end": v(-11518.37, -20889.75) * mm});
            skLineSegment(sketch, "E194.left", {"start": v(-14518.37, -18889.75) * mm, "end": v(-14518.37, -20889.75) * mm});
            skLineSegment(sketch, "E194.right", {"start": v(-11518.37, -18889.75) * mm, "end": v(-11518.37, -20889.75) * mm});
            skText(sketch, "E195", { "text": "Hyd.\nPress", "fontName": "OpenSans-Regular.ttf"});
            skText(sketch, "E196", { "text": "Wheel Shop", "fontName": "OpenSans-Regular.ttf"});
            const initialGuessF2  = {"E7": [9.38992, -5.54064, 0, -1, 1], "E8": [9.4982, 7.11065, 0, -1, 1], "E9": [9.51077, 19.3744, 0, -1, 1], "E12": [3.88006, 13.617, 1, 0, 1], "E38": [-13.83839, 21.90066, 1, 0, 1], "E41": [-9.70286, 22.85873, 1, 0, 1], "E45": [-9.66514, 20.48987, 1, 0, 1], "E78": [-12.35316, 15.24984, 1, 0, 0.5097], "E92": [-13.93936, 11.61546, 1, 0, 0.5097], "E93": [-8.7623, 12.6893, 0, -1, 0.56413], "E94": [-5.82773, 12.66575, 0, -1, 0.56413], "E98": [-14.40656, 3.15847, 1, 0, 0.5097], "E103": [-4.16474, 4.84222, 0, -1, 0.5097], "E104": [-8.71916, 2.98794, 1, 0, 0.5097], "E106": [0.08069, 3.79994, 0, -1, 1.5158], "E107": [0.16145, -13.632, 0, -1, 1], "E119": [-11.21941, -0.47049, 0, -1, 0.64522], "E123": [-7.25972, -1.13238, 0, -1, 0.64522], "E128": [-3.89123, -7.8332, 0, -1, 0.5], "E130": [-5.86612, -8.68905, 1, 0, 0.5], "E132": [-8.18048, -8.57776, 1, 0, 0.5], "E141": [-13.26716, -9.94748, 1, 0, 0.5], "E143": [-14.7599, -13.02777, 1, 0, 0.5], "E150": [-8.12603, -12.78329, 1, 0, 0.5], "E152": [-6.23332, -12.76148, 1, 0, 0.5], "E154": [-4.32764, -12.22573, 1, 0, 0.5], "E162": [-6.16341, 23.75566, 0, -1, 0.56413], "E163": [-2.12558, 23.80624, 0, -1, 0.56413], "E164": [1.6559, 23.77153, 0, -1, 0.5], "E165": [1.64387, 16.387, 0, -1, 0.5], "E169": [-4.42864, -1.40399, 0, -1, 0.64522], "E171": [-5.85026, 0.4145, 1, 0, 0.56818], "E179": [-13.79004, -16.51483, 1, 0, 0.5], "E181": [-9.6014, -18.05704, 1, 0, 0.5], "E183": [-8.50162, -15.24363, 1, 0, 0.5], "E185": [-4.7922, -17.13952, 1, 0, 0.5], "E186": [-10.25634, -16.7267, 1, 0, 0.5], "E187": [-11.15678, -6.71997, 1, 0, 0.5], "E189": [-9.04742, -20.0199, 1, 0, 0.5], "E191": [-13.25243, -24.11773, 1, 0, 0.4747], "E193": [-7.53651, -24.606, 1, 0, 0.46114], "E195": [-14.0772, -19.61483, 1, 0, 0.56964], "E196": [-11.8186, -22.289, 1, 0, 0.78206]};
            skSetInitialGuess(sketch, initialGuessF2);
            skSolve(sketch);
        }
        {
            var Q0;
            {var subQ12=sQuery(id+"F2.wireOp",EDGE,"E23");Q0=makeQuery(id+"F2.imprint","IMPRINT",FACE,{"disambiguationData":[TD([[makeQuery(id+"F2.imprint","IMPRINT",EDGE,{"derivedFrom":subQ12}),1.0]])]});}
            var Q1;
            {var subQ0=sQuery(id+"F2.wireOp",EDGE,"E19.0");var subQ1=sQuery(id+"F2.wireOp",EDGE,"E10");var subQ2=makeQuery(id+"F2.imprint","INTERSECT",VERTEX,{"derivedFrom":[subQ1,subQ0]});Q1=makeQuery(id+"F2.imprint","IMPRINT",FACE,{"disambiguationData":[TD([[makeQuery(id+"F2.imprint","IMPRINT",EDGE,{"disambiguationData":[TD([[subQ2,1.0]])],"derivedFrom":subQ1}),-1.0]])]});}
            var Q2;
            {var subQ13=sQuery(id+"F2.wireOp",EDGE,"E5");Q2=makeQuery(id+"F2.imprint","IMPRINT",FACE,{"disambiguationData":[TD([[makeQuery(id+"F2.imprint","IMPRINT",EDGE,{"derivedFrom":subQ13}),1.0]])]});}
            var Q3;
            {var subQ0=sQuery(id+"F2.wireOp",EDGE,"E28");var subQ1=sQuery(id+"F2.wireOp",EDGE,"E22");var subQ2=makeQuery(id+"F2.imprint","INTERSECT",VERTEX,{"derivedFrom":[subQ1,subQ0]});Q3=makeQuery(id+"F2.imprint","IMPRINT",FACE,{"disambiguationData":[TD([[makeQuery(id+"F2.imprint","IMPRINT",EDGE,{"disambiguationData":[TD([[subQ2,1.0]])],"derivedFrom":subQ1}),-1.0]])]});}
            var Q4;
            {var subQ0=sQuery(id+"F2.wireOp",EDGE,"E28");var subQ1=sQuery(id+"F2.wireOp",EDGE,"E10");var subQ2=makeQuery(id+"F2.imprint","INTERSECT",VERTEX,{"derivedFrom":[subQ1,subQ0]});Q4=makeQuery(id+"F2.imprint","IMPRINT",FACE,{"disambiguationData":[TD([[makeQuery(id+"F2.imprint","IMPRINT",EDGE,{"disambiguationData":[TD([[subQ2,-1.0]])],"derivedFrom":subQ1}),-1.0]])]});}
            var Q5;
            {var subQ0=sQuery(id+"F2.wireOp",EDGE,"E29.0");var subQ1=sQuery(id+"F2.wireOp",EDGE,"E17");var subQ2=makeQuery(id+"F2.imprint","INTERSECT",VERTEX,{"derivedFrom":[subQ1,subQ0]});Q5=makeQuery(id+"F2.imprint","IMPRINT",FACE,{"disambiguationData":[TD([[makeQuery(id+"F2.imprint","IMPRINT",EDGE,{"disambiguationData":[TD([[subQ2,-1.0]])],"derivedFrom":subQ1}),-1.0]])]});}
            var Q6;
            {var subQ1=sQuery(id+"F2.wireOp",EDGE,"E95");Q6=makeQuery(id+"F2.imprint","IMPRINT",FACE,{"disambiguationData":[TD([[makeQuery(id+"F2.imprint","IMPRINT",EDGE,{"derivedFrom":subQ1}),1.0]])]});}
            var Q7;
            {var subQ0=sQuery(id+"F2.wireOp",EDGE,"E97");Q7=makeQuery(id+"F2.imprint","IMPRINT",FACE,{"disambiguationData":[TD([[makeQuery(id+"F2.imprint","IMPRINT",EDGE,{"derivedFrom":subQ0}),1.0]])]});}
            var Q8;
            {var subQ0=sQuery(id+"F2.wireOp",EDGE,"E25.trimOffspring");var subQ1=sQuery(id+"F2.wireOp",EDGE,"E17");var subQ2=makeQuery(id+"F2.imprint","INTERSECT",VERTEX,{"derivedFrom":[subQ1,subQ0]});Q8=makeQuery(id+"F2.imprint","IMPRINT",FACE,{"disambiguationData":[TD([[makeQuery(id+"F2.imprint","IMPRINT",EDGE,{"disambiguationData":[TD([[subQ2,1.0]])],"derivedFrom":subQ1}),-1.0]])]});}
            var Q9;
            {var subQ0=sQuery(id+"F2.wireOp",EDGE,"E25.trimOffspring");var subQ1=sQuery(id+"F2.wireOp",EDGE,"E18.0");var subQ2=makeQuery(id+"F2.imprint","INTERSECT",VERTEX,{"derivedFrom":[subQ1,subQ0]});Q9=makeQuery(id+"F2.imprint","IMPRINT",FACE,{"disambiguationData":[TD([[makeQuery(id+"F2.imprint","IMPRINT",EDGE,{"disambiguationData":[TD([[subQ2,1.0]])],"derivedFrom":subQ1}),-1.0]])]});}
            var Q10;
            {var subQ0=sQuery(id+"F2.wireOp",EDGE,"E25.trimOffspring");var subQ1=sQuery(id+"F2.wireOp",EDGE,"E17");var subQ2=makeQuery(id+"F2.imprint","INTERSECT",VERTEX,{"derivedFrom":[subQ1,subQ0]});Q10=makeQuery(id+"F2.imprint","IMPRINT",FACE,{"disambiguationData":[TD([[makeQuery(id+"F2.imprint","IMPRINT",EDGE,{"disambiguationData":[TD([[subQ2,1.0]])],"derivedFrom":subQ1}),1.0]])]});}
            var Q11;
            {var subQ0=sQuery(id+"F2.wireOp",EDGE,"E29.0");var subQ1=sQuery(id+"F2.wireOp",EDGE,"E18.0");var subQ2=makeQuery(id+"F2.imprint","INTERSECT",VERTEX,{"derivedFrom":[subQ1,subQ0]});Q11=makeQuery(id+"F2.imprint","IMPRINT",FACE,{"disambiguationData":[TD([[makeQuery(id+"F2.imprint","IMPRINT",EDGE,{"disambiguationData":[TD([[subQ2,-1.0]])],"derivedFrom":subQ1}),-1.0]])]});}
            var Q12;
            {var subQ0=sQuery(id+"F2.wireOp",EDGE,"E29.0");var subQ1=sQuery(id+"F2.wireOp",EDGE,"E17");var subQ2=makeQuery(id+"F2.imprint","INTERSECT",VERTEX,{"derivedFrom":[subQ1,subQ0]});Q12=makeQuery(id+"F2.imprint","IMPRINT",FACE,{"disambiguationData":[TD([[makeQuery(id+"F2.imprint","IMPRINT",EDGE,{"disambiguationData":[TD([[subQ2,-1.0]])],"derivedFrom":subQ1}),1.0]])]});}
            extrude(context, id + "F3", {"entities" : qUnion([Q0, Q1, Q2, Q3, Q4, Q5, Q6, Q7, Q8, Q9, Q10, Q11, Q12]), "depth" : 25 * mm, "offsetDistance" : 25 * mm});
        }
    });